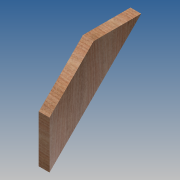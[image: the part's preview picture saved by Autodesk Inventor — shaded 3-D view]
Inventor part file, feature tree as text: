
AUTODESK INVENTOR PART (.ipt)
format: ipt  version: 2013 (Build 170138000, 138)  size: 85,504 bytes
history: native  units: in
note: dims shown in document units (in); Inventor stores cm internally (conversion verified against a paired STEP export)
features: extrude x1, sketch x1
ambient origin geometry x8: Origin, YZ Plane, XZ Plane, XY Plane, X Axis, Y Axis, Z Axis, Center Point
bodies: Solid1 (feature_tree)
feature tree (2):
  extrude  "Extrusion1"  TaperAngle=45.0deg  [1 undecoded]
  sketch  "Sketch1"  dims[d0=12.0in d1=45.0deg d2=5.5in d3=1.75in d4=0.0in d5=15.0in]
note: 1 required parameter value undecoded (feature->parameter linkage not recoverable at this tier; creation-order binding heuristic only, values carry confidence <= 0.55)
